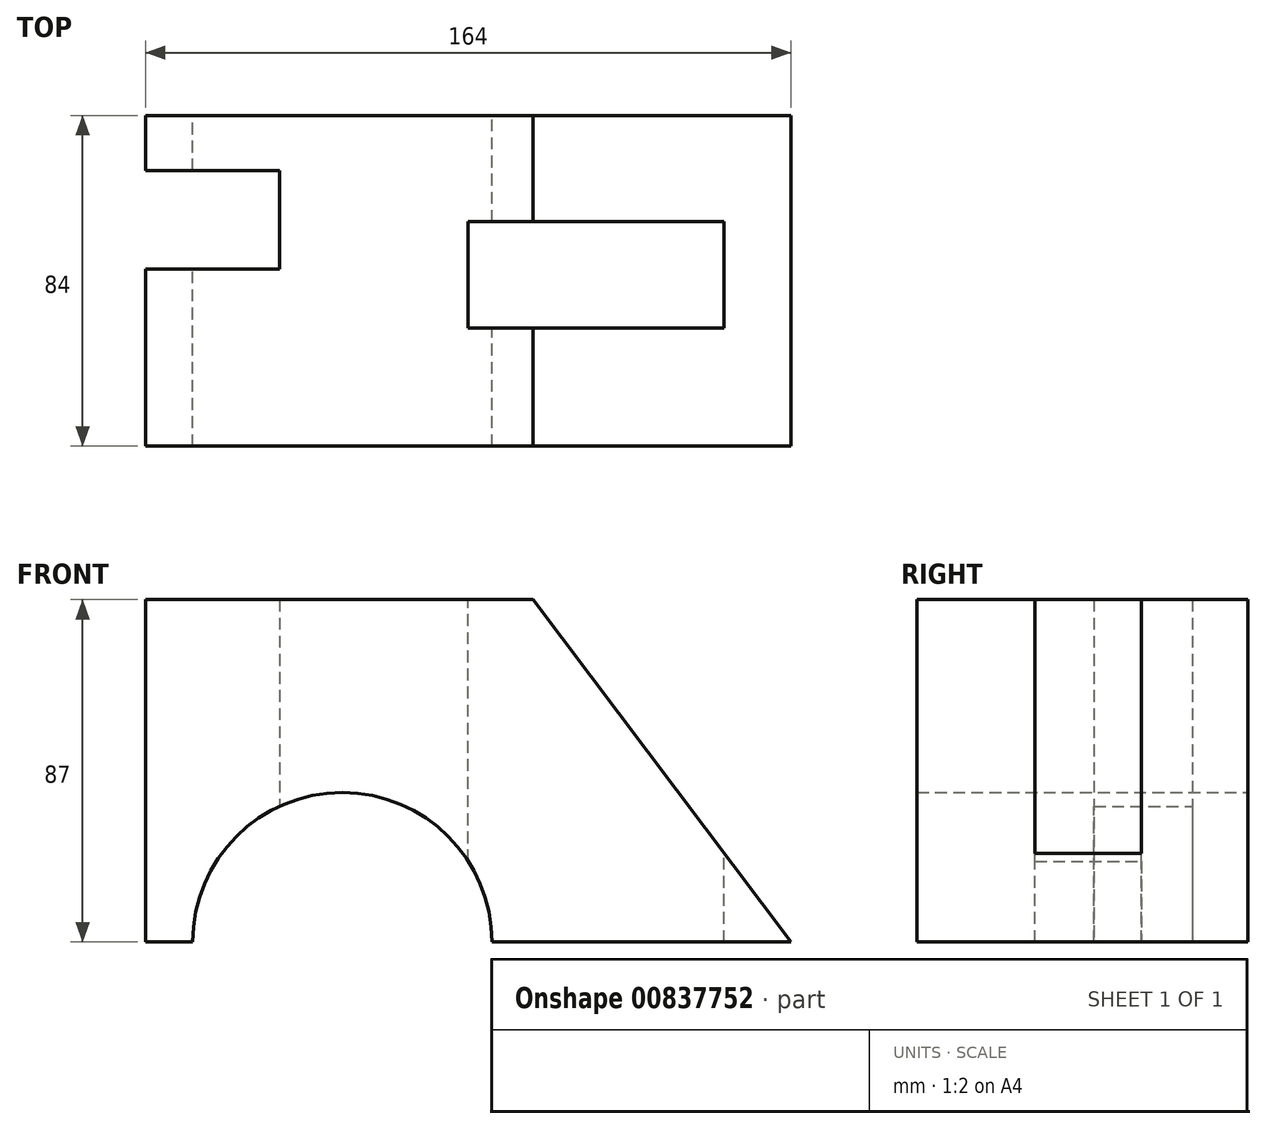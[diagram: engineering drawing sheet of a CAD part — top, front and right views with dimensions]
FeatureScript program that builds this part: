
annotation { "Feature Type Name" : "Feature", "Feature Type Description" : "" }
export const myFeature = defineFeature(function(context is Context, id is Id, definition is map)
    precondition{}
    {
        {
            var Q0;
            Q0=qCreatedBy(makeId("Front.planeOp"),FACE);
            var sketch = newSketch(context, id + "F0", { "sketchPlane" : qUnion([Q0])});
            skLineSegment(sketch, "E0.bottom", {"start": v(-82, 45.62) * mm, "end": v(16.44, 45.62) * mm});
            skLineSegment(sketch, "E0.top", {"start": v(-82, -41.38) * mm, "end": v(82, -41.38) * mm});
            skLineSegment(sketch, "E0.left", {"start": v(-82, 45.62) * mm, "end": v(-82, -41.38) * mm});
            skPoint(sketch, "E0.middle", {"position": v(0, 2.12) * mm});
            skLineSegment(sketch, "E1", {"start": v(-82, -41.38) * mm, "end": v(-32, -41.38) * mm});
            skArc(sketch, "E2", {"start": v(6, -41.38) * mm, "mid": v(-32, -3.38) * mm, "end": v(-70, -41.38) * mm});
            skLineSegment(sketch, "E3", {"start": v(0, 45.62) * mm, "end": v(16.44, 45.62) * mm});
            skLineSegment(sketch, "E4", {"start": v(16.44, 45.62) * mm, "end": v(82, -41.38) * mm});
            skPoint(sketch, "E0.right.start.orphan", {"position": v(82, 45.62) * mm});
            skSolve(sketch);
        }
        {
            var Q0;
            Q0=makeQuery(id+"F0.imprint","IMPRINT",FACE,{"disambiguationData":[TD([[makeQuery(id+"F0.imprint","IMPRINT",EDGE,{"derivedFrom":sQuery(id+"F0.wireOp",EDGE,"E0.bottom")}),-1.0]])]});
            extrude(context, id + "F1", {"entities" : qUnion([Q0]), "depth" : 84 * mm, "offsetDistance" : 25 * mm});
        }
        {
            var Q0;
            Q0=qCreatedBy(makeId("Top.planeOp"),FACE);
            var sketch = newSketch(context, id + "F2", { "sketchPlane" : qUnion([Q0])});
            skLineSegment(sketch, "E5.0.0", {"start": v(16.44, 0) * mm, "end": v(-82, 0) * mm});
            skLineSegment(sketch, "E5.0.1", {"start": v(-82, 0) * mm, "end": v(-82, -84) * mm});
            skLineSegment(sketch, "E5.0.2", {"start": v(-82, -84) * mm, "end": v(16.44, -84) * mm});
            skLineSegment(sketch, "E5.0.3", {"start": v(16.44, -84) * mm, "end": v(16.44, 0) * mm});
            skLineSegment(sketch, "E6", {"start": v(-82, 0) * mm, "end": v(-82, -14) * mm});
            skLineSegment(sketch, "E7", {"start": v(-82, -14) * mm, "end": v(-82, -39) * mm});
            skLineSegment(sketch, "E8", {"start": v(-82, -39) * mm, "end": v(-48, -39) * mm});
            skLineSegment(sketch, "E9", {"start": v(-48, -39) * mm, "end": v(-48, -14) * mm});
            skLineSegment(sketch, "E10", {"start": v(-48, -14) * mm, "end": v(-82, -14) * mm});
            skSolve(sketch);
        }
        {
            var Q0;
            {var subQ0=sQuery(id+"F2.wireOp",EDGE,"E8");Q0=makeQuery(id+"F2.imprint","IMPRINT",FACE,{"disambiguationData":[TD([[makeQuery(id+"F2.imprint","IMPRINT",EDGE,{"derivedFrom":subQ0}),1.0]])]});}
            var Q1;
            Q1=sQuery(id+"F2.wireOp",EDGE,"E10");
            var Q2;
            Q2=sQuery(id+"F2.wireOp",EDGE,"E9");
            var Q3;
            Q3=sQuery(id+"F2.wireOp",EDGE,"E7");
            var Q4;
            Q4=sQuery(id+"F2.wireOp",EDGE,"E8");
            extrude(context, id + "F3", {"entities" : qUnion([Q0]), "operationType" : NewBodyOperationType.REMOVE, "surfaceEntities" : qUnion([Q1, Q2, Q3, Q4]), "depth" : 94.8 * mm, "offsetDistance" : 25 * mm, "hasSecondDirection" : true, "secondDirectionOppositeDirection" : true, "secondDirectionDepth" : 151.8 * mm});
        }
        {
            var Q0;
            Q0=makeQuery(id+"F1.opExtrude","SWEPT_FACE",FACE,{"disambiguationData":[OSD([sQuery(id+"F0.wireOp",EDGE,"E0.bottom"),sQuery(id+"F0.wireOp",EDGE,"E3")])]});
            var sketch = newSketch(context, id + "F4", { "sketchPlane" : qUnion([Q0])});
            skLineSegment(sketch, "E11", {"start": v(0, 0) * mm, "end": v(0, -27) * mm});
            skLineSegment(sketch, "E12", {"start": v(0, -27) * mm, "end": v(0, -54) * mm});
            skLineSegment(sketch, "E13", {"start": v(0, -54) * mm, "end": v(65, -54) * mm});
            skLineSegment(sketch, "E14", {"start": v(65, -54) * mm, "end": v(65, -27) * mm});
            skLineSegment(sketch, "E15", {"start": v(65, -27) * mm, "end": v(0, -27) * mm});
            skSolve(sketch);
        }
        {
            var Q0;
            {var subQ0=sQuery(id+"F4.wireOp",EDGE,"E14");Q0=makeQuery(id+"F4.imprint","IMPRINT",FACE,{"disambiguationData":[TD([[makeQuery(id+"F4.imprint","IMPRINT",EDGE,{"derivedFrom":subQ0}),1.0]])]});}
            var Q1;
            {var subQ0=sQuery(id+"F4.wireOp",EDGE,"E12");Q1=makeQuery(id+"F4.imprint","IMPRINT",FACE,{"disambiguationData":[TD([[makeQuery(id+"F4.imprint","IMPRINT",EDGE,{"derivedFrom":subQ0}),1.0]])]});}
            extrude(context, id + "F5", {"entities" : qUnion([Q0, Q1]), "operationType" : NewBodyOperationType.REMOVE, "oppositeDirection" : true, "depth" : 360.4 * mm, "offsetDistance" : 25 * mm});
        }
    });
